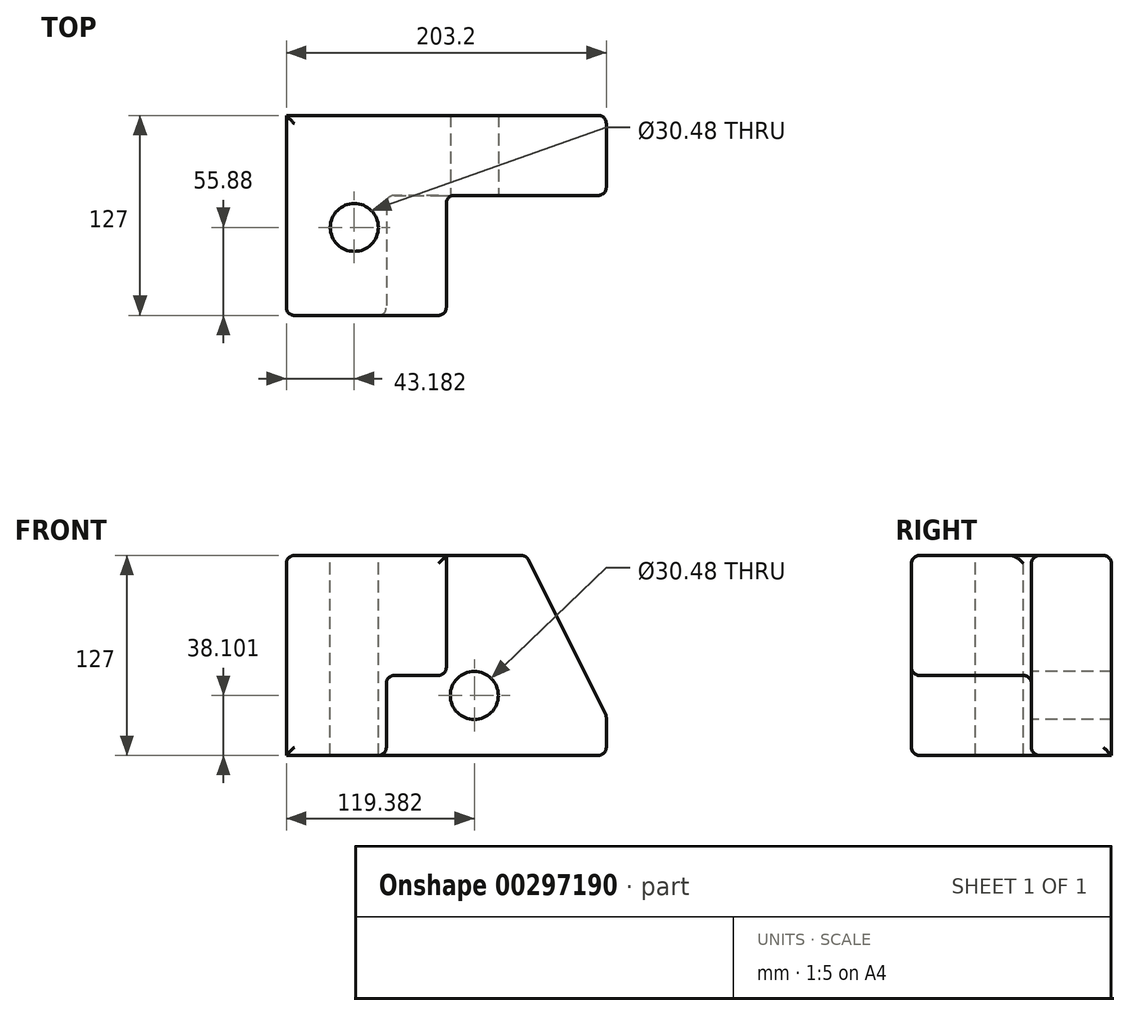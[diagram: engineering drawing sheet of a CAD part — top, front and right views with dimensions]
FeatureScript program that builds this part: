
annotation { "Feature Type Name" : "Feature", "Feature Type Description" : "" }
export const myFeature = defineFeature(function(context is Context, id is Id, definition is map)
    precondition{}
    {
        {
            var Q0;
            Q0=qCreatedBy(makeId("Front.planeOp"),FACE);
            var sketch = newSketch(context, id + "F0", { "sketchPlane" : qUnion([Q0])});
            skLineSegment(sketch, "E0.bottom", {"start": v(-100.19, 51.27) * mm, "end": v(103.01, 51.27) * mm});
            skLineSegment(sketch, "E0.top", {"start": v(-100.19, -75.73) * mm, "end": v(103.01, -75.73) * mm});
            skLineSegment(sketch, "E0.left", {"start": v(-100.19, 51.27) * mm, "end": v(-100.19, -75.73) * mm});
            skLineSegment(sketch, "E0.right", {"start": v(103.01, 51.27) * mm, "end": v(103.01, -75.73) * mm});
            skSolve(sketch);
        }
        {
            var Q0;
            Q0 = qSketchRegion(id + "F0", true);
            extrude(context, id + "F1", {"entities" : qUnion([Q0]), "depth" : 127 * mm});
        }
        {
            var Q0;
            Q0=makeQuery(id+"F1.opExtrude","CAP_FACE",FACE,{"disambiguationData":[OSD([sQuery(id+"F0.wireOp",EDGE,"E0.bottom"),sQuery(id+"F0.wireOp",EDGE,"E0.top"),sQuery(id+"F0.wireOp",EDGE,"E0.left"),sQuery(id+"F0.wireOp",EDGE,"E0.right")])],"isStart":false});
            var sketch = newSketch(context, id + "F2", { "sketchPlane" : qUnion([Q0])});
            skLineSegment(sketch, "E1", {"start": v(-100.19, -75.73) * mm, "end": v(-100.19, 51.27) * mm});
            skLineSegment(sketch, "E2", {"start": v(-100.19, 51.27) * mm, "end": v(1.41, 51.27) * mm});
            skLineSegment(sketch, "E3", {"start": v(1.41, 51.27) * mm, "end": v(1.41, -24.93) * mm});
            skLineSegment(sketch, "E4", {"start": v(1.41, -24.93) * mm, "end": v(-36.69, -24.93) * mm});
            skLineSegment(sketch, "E5", {"start": v(-36.69, -24.93) * mm, "end": v(-36.69, -75.73) * mm});
            skLineSegment(sketch, "E6", {"start": v(-36.69, -75.73) * mm, "end": v(-100.19, -75.73) * mm});
            skSolve(sketch);
        }
        {
            var Q0;
            {var subQ2=sQuery(id+"F2.wireOp",EDGE,"E3");Q0=makeQuery(id+"F2.imprint","IMPRINT",FACE,{"disambiguationData":[TD([[makeQuery(id+"F2.imprint","IMPRINT",EDGE,{"derivedFrom":subQ2}),1.0]])]});}
            extrude(context, id + "F3", {"entities" : qUnion([Q0]), "operationType" : NewBodyOperationType.REMOVE, "oppositeDirection" : true, "depth" : 76.2 * mm});
        }
        {
            var Q0;
            Q0=makeQuery(id+"F1.opExtrude","SWEPT_EDGE",EDGE,{"disambiguationData":[OSD([sQuery(id+"F0.wireOp",EDGE,"E0.bottom"),sQuery(id+"F0.wireOp",EDGE,"E0.right")])]});
            chamfer(context, id + "F4", {"entities" : qUnion([Q0]), "chamferType" : ChamferType.TWO_OFFSETS, "width1" : 50.8 * mm, "oppositeDirection" : false, "width2" : 101.6 * mm, "tangentPropagation" : true});
        }
        {
            var Q0;
            Q0=makeQuery(id+"F1.opExtrude","CAP_EDGE",EDGE,{"disambiguationData":[OSD([sQuery(id+"F0.wireOp",EDGE,"E0.bottom")])],"isStart":false});
            var Q1;
            Q1=makeQuery(id+"F1.opExtrude","SWEPT_EDGE",EDGE,{"disambiguationData":[OSD([sQuery(id+"F0.wireOp",EDGE,"E0.bottom"),sQuery(id+"F0.wireOp",EDGE,"E0.left")])]});
            var Q2;
            Q2=makeQuery(id+"F3.boolean.opBoolean","COPY",EDGE,{"derivedFrom":makeQuery(id+"F3.opExtrude","SWEPT_EDGE",EDGE,{"disambiguationData":[OSD([sQuery(id+"F0.wireOp",EDGE,"E0.bottom"),sQuery(id+"F2.wireOp",EDGE,"E2"),sQuery(id+"F2.wireOp",EDGE,"E3")])]})});
            var Q3;
            Q3=makeQuery(id+"F3.boolean.opBoolean","COPY",EDGE,{"derivedFrom":makeQuery(id+"F3.opExtrude","CAP_EDGE",EDGE,{"disambiguationData":[OSD([sQuery(id+"F0.wireOp",EDGE,"E0.bottom")])],"isStart":false})});
            var Q4;
            {var subQ0=sQuery(id+"F0.wireOp",EDGE,"E0.bottom");Q4=makeQuery(id+"F4.opChamfer","BLEND_EDGE",EDGE,{"blendedFrom":[makeQuery(id+"F1.opExtrude","SWEPT_EDGE",EDGE,{"disambiguationData":[OSD([subQ0,sQuery(id+"F0.wireOp",EDGE,"E0.right")])]}),makeQuery(id+"F1.opExtrude","SWEPT_FACE",FACE,{"disambiguationData":[OSD([subQ0])]})],"blendedInto":[makeQuery(id+"F1.opExtrude","SWEPT_FACE",FACE,{"disambiguationData":[OSD([subQ0])]})]});}
            var Q5;
            Q5=makeQuery(id+"F1.opExtrude","CAP_EDGE",EDGE,{"disambiguationData":[OSD([sQuery(id+"F0.wireOp",EDGE,"E0.bottom")])],"isStart":true});
            var Q6;
            {var subQ0=sQuery(id+"F0.wireOp",EDGE,"E0.right");var subQ1=sQuery(id+"F0.wireOp",EDGE,"E0.bottom");Q6=makeQuery(id+"F4.opChamfer","BLEND_EDGE",EDGE,{"blendedFrom":[makeQuery(id+"F1.opExtrude","SWEPT_EDGE",EDGE,{"disambiguationData":[OSD([subQ1,subQ0])]}),makeQuery(id+"F3.boolean.opBoolean","COPY",FACE,{"derivedFrom":makeQuery(id+"F3.opExtrude","CAP_FACE",FACE,{"disambiguationData":[OSD([subQ1,sQuery(id+"F0.wireOp",EDGE,"E0.top"),subQ0,sQuery(id+"F2.wireOp",EDGE,"E3"),sQuery(id+"F2.wireOp",EDGE,"E4"),sQuery(id+"F2.wireOp",EDGE,"E5")])],"isStart":false})})],"blendedInto":[makeQuery(id+"F3.boolean.opBoolean","COPY",FACE,{"derivedFrom":makeQuery(id+"F3.opExtrude","CAP_FACE",FACE,{"disambiguationData":[OSD([subQ1,sQuery(id+"F0.wireOp",EDGE,"E0.top"),subQ0,sQuery(id+"F2.wireOp",EDGE,"E3"),sQuery(id+"F2.wireOp",EDGE,"E4"),sQuery(id+"F2.wireOp",EDGE,"E5")])],"isStart":false})})]});}
            var Q7;
            {var subQ0=sQuery(id+"F0.wireOp",EDGE,"E0.right");var subQ1=sQuery(id+"F0.wireOp",EDGE,"E0.bottom");Q7=makeQuery(id+"F4.opChamfer","BLEND_EDGE",EDGE,{"blendedFrom":[makeQuery(id+"F1.opExtrude","SWEPT_EDGE",EDGE,{"disambiguationData":[OSD([subQ1,subQ0])]}),makeQuery(id+"F1.opExtrude","CAP_FACE",FACE,{"disambiguationData":[OSD([subQ1,sQuery(id+"F0.wireOp",EDGE,"E0.top"),sQuery(id+"F0.wireOp",EDGE,"E0.left"),subQ0])],"isStart":true})],"blendedInto":[makeQuery(id+"F1.opExtrude","CAP_FACE",FACE,{"disambiguationData":[OSD([subQ1,sQuery(id+"F0.wireOp",EDGE,"E0.top"),sQuery(id+"F0.wireOp",EDGE,"E0.left"),subQ0])],"isStart":true})]});}
            var Q8;
            {var subQ0=sQuery(id+"F0.wireOp",EDGE,"E0.right");Q8=makeQuery(id+"F4.opChamfer","BLEND_EDGE",EDGE,{"blendedFrom":[makeQuery(id+"F1.opExtrude","SWEPT_EDGE",EDGE,{"disambiguationData":[OSD([sQuery(id+"F0.wireOp",EDGE,"E0.bottom"),subQ0])]}),makeQuery(id+"F1.opExtrude","SWEPT_FACE",FACE,{"disambiguationData":[OSD([subQ0])]})],"blendedInto":[makeQuery(id+"F1.opExtrude","SWEPT_FACE",FACE,{"disambiguationData":[OSD([subQ0])]})]});}
            var Q9;
            Q9=makeQuery(id+"F1.opExtrude","SWEPT_FACE",FACE,{"disambiguationData":[OSD([sQuery(id+"F0.wireOp",EDGE,"E0.right")])]});
            var Q10;
            Q10=makeQuery(id+"F3.boolean.opBoolean","COPY",EDGE,{"derivedFrom":makeQuery(id+"F3.opExtrude","CAP_EDGE",EDGE,{"disambiguationData":[OSD([sQuery(id+"F0.wireOp",EDGE,"E0.right")])],"isStart":false})});
            var Q11;
            Q11=makeQuery(id+"F1.opExtrude","CAP_EDGE",EDGE,{"disambiguationData":[OSD([sQuery(id+"F0.wireOp",EDGE,"E0.right")])],"isStart":true});
            var Q12;
            Q12=makeQuery(id+"F3.boolean.opBoolean","COPY",EDGE,{"derivedFrom":makeQuery(id+"F3.opExtrude","CAP_EDGE",EDGE,{"disambiguationData":[OSD([sQuery(id+"F0.wireOp",EDGE,"E0.top")])],"isStart":false})});
            var Q13;
            Q13=makeQuery(id+"F3.boolean.opBoolean","COPY",EDGE,{"derivedFrom":makeQuery(id+"F3.opExtrude","CAP_EDGE",EDGE,{"disambiguationData":[OSD([sQuery(id+"F2.wireOp",EDGE,"E3")])],"isStart":false})});
            var Q14;
            Q14=makeQuery(id+"F3.boolean.opBoolean","COPY",EDGE,{"derivedFrom":makeQuery(id+"F3.opExtrude","SWEPT_EDGE",EDGE,{"disambiguationData":[OSD([sQuery(id+"F2.wireOp",EDGE,"E3"),sQuery(id+"F2.wireOp",EDGE,"E4")])]})});
            var Q15;
            Q15=makeQuery(id+"F3.boolean.opBoolean","COPY",EDGE,{"derivedFrom":makeQuery(id+"F3.opExtrude","CAP_EDGE",EDGE,{"disambiguationData":[OSD([sQuery(id+"F2.wireOp",EDGE,"E5")])],"isStart":false})});
            var Q16;
            Q16=makeQuery(id+"F3.boolean.opBoolean","COPY",EDGE,{"derivedFrom":makeQuery(id+"F3.opExtrude","CAP_EDGE",EDGE,{"disambiguationData":[OSD([sQuery(id+"F2.wireOp",EDGE,"E4")])],"isStart":true})});
            var Q17;
            Q17=makeQuery(id+"F3.boolean.opBoolean","COPY",EDGE,{"derivedFrom":makeQuery(id+"F3.opExtrude","CAP_EDGE",EDGE,{"disambiguationData":[OSD([sQuery(id+"F2.wireOp",EDGE,"E5")])],"isStart":true})});
            var Q18;
            Q18=makeQuery(id+"F1.opExtrude","CAP_EDGE",EDGE,{"disambiguationData":[OSD([sQuery(id+"F0.wireOp",EDGE,"E0.top")])],"isStart":false});
            var Q19;
            Q19=makeQuery(id+"F3.boolean.opBoolean","COPY",EDGE,{"derivedFrom":makeQuery(id+"F3.opExtrude","SWEPT_EDGE",EDGE,{"disambiguationData":[OSD([sQuery(id+"F0.wireOp",EDGE,"E0.top"),sQuery(id+"F2.wireOp",EDGE,"E5"),sQuery(id+"F2.wireOp",EDGE,"E6")])]})});
            var Q20;
            Q20=makeQuery(id+"F3.boolean.opBoolean","COPY",FACE,{"derivedFrom":makeQuery(id+"F3.opExtrude","CAP_FACE",FACE,{"disambiguationData":[OSD([sQuery(id+"F0.wireOp",EDGE,"E0.bottom"),sQuery(id+"F0.wireOp",EDGE,"E0.top"),sQuery(id+"F0.wireOp",EDGE,"E0.right"),sQuery(id+"F2.wireOp",EDGE,"E3"),sQuery(id+"F2.wireOp",EDGE,"E4"),sQuery(id+"F2.wireOp",EDGE,"E5")])],"isStart":false})});
            var Q21;
            Q21=makeQuery(id+"F3.boolean.opBoolean","COPY",FACE,{"derivedFrom":makeQuery(id+"F3.opExtrude","SWEPT_FACE",FACE,{"disambiguationData":[OSD([sQuery(id+"F2.wireOp",EDGE,"E5")])]})});
            var Q22;
            Q22=makeQuery(id+"F1.opExtrude","CAP_EDGE",EDGE,{"disambiguationData":[OSD([sQuery(id+"F0.wireOp",EDGE,"E0.left")])],"isStart":false});
            var Q23;
            Q23=makeQuery(id+"F1.opExtrude","CAP_FACE",FACE,{"disambiguationData":[OSD([sQuery(id+"F0.wireOp",EDGE,"E0.bottom"),sQuery(id+"F0.wireOp",EDGE,"E0.top"),sQuery(id+"F0.wireOp",EDGE,"E0.left"),sQuery(id+"F0.wireOp",EDGE,"E0.right")])],"isStart":false});
            var Q24;
            Q24=makeQuery(id+"F3.boolean.opBoolean","COPY",EDGE,{"derivedFrom":makeQuery(id+"F3.opExtrude","CAP_EDGE",EDGE,{"disambiguationData":[OSD([sQuery(id+"F2.wireOp",EDGE,"E3")])],"isStart":true})});
            fillet(context, id + "F5", {"entities" : qUnion([Q0, Q1, Q2, Q3, Q4, Q5, Q6, Q7, Q8, Q9, Q10, Q11, Q12, Q13, Q14, Q15, Q16, Q17, Q18, Q19, Q20, Q21, Q22, Q23, Q24]), "radius" : 5.08 * mm, "tangentPropagation" : true, "allowEdgeOverflow" : false});
        }
        {
            var Q0;
            Q0=makeQuery(id+"F3.boolean.opBoolean","COPY",FACE,{"derivedFrom":makeQuery(id+"F3.opExtrude","CAP_FACE",FACE,{"disambiguationData":[OSD([sQuery(id+"F0.wireOp",EDGE,"E0.bottom"),sQuery(id+"F0.wireOp",EDGE,"E0.top"),sQuery(id+"F0.wireOp",EDGE,"E0.right"),sQuery(id+"F2.wireOp",EDGE,"E3"),sQuery(id+"F2.wireOp",EDGE,"E4"),sQuery(id+"F2.wireOp",EDGE,"E5")])],"isStart":false})});
            var sketch = newSketch(context, id + "F6", { "sketchPlane" : qUnion([Q0])});
            skCircle(sketch, "E7", {"center": v(19.2, -37.63) * mm, "radius": 15.24 * mm});
            skSolve(sketch);
        }
        {
            var Q0;
            Q0=makeQuery(id+"F6.imprint","IMPRINT",FACE,{"disambiguationData":[TD([[makeQuery(id+"F6.imprint","IMPRINT",EDGE,{"derivedFrom":sQuery(id+"F6.wireOp",EDGE,"E7")}),1.0]])]});
            var Q1;
            Q1=makeQuery(id+"F1.opExtrude","CAP_FACE",FACE,{"disambiguationData":[OSD([sQuery(id+"F0.wireOp",EDGE,"E0.bottom"),sQuery(id+"F0.wireOp",EDGE,"E0.top"),sQuery(id+"F0.wireOp",EDGE,"E0.left"),sQuery(id+"F0.wireOp",EDGE,"E0.right")])],"isStart":true});
            extrude(context, id + "F7", {"entities" : qUnion([Q0]), "operationType" : NewBodyOperationType.REMOVE, "endBound" : BoundingType.UP_TO_SURFACE, "oppositeDirection" : true, "endBoundEntityFace" : qUnion([Q1]), "depth" : 25.4 * mm});
        }
        {
            var Q0;
            Q0=makeQuery(id+"F1.opExtrude","SWEPT_FACE",FACE,{"disambiguationData":[OSD([sQuery(id+"F0.wireOp",EDGE,"E0.bottom")])]});
            var sketch = newSketch(context, id + "F8", { "sketchPlane" : qUnion([Q0])});
            skCircle(sketch, "E8", {"center": v(-57, -71.12) * mm, "radius": 15.24 * mm});
            skSolve(sketch);
        }
        {
            var Q0;
            Q0=makeQuery(id+"F8.imprint","IMPRINT",FACE,{"disambiguationData":[TD([[makeQuery(id+"F8.imprint","IMPRINT",EDGE,{"derivedFrom":sQuery(id+"F8.wireOp",EDGE,"E8")}),1.0]])]});
            var Q1;
            Q1=makeQuery(id+"F1.opExtrude","SWEPT_FACE",FACE,{"disambiguationData":[OSD([sQuery(id+"F0.wireOp",EDGE,"E0.top")])]});
            extrude(context, id + "F9", {"entities" : qUnion([Q0]), "operationType" : NewBodyOperationType.REMOVE, "endBound" : BoundingType.UP_TO_SURFACE, "oppositeDirection" : true, "endBoundEntityFace" : qUnion([Q1]), "depth" : 25.4 * mm});
        }
    });
